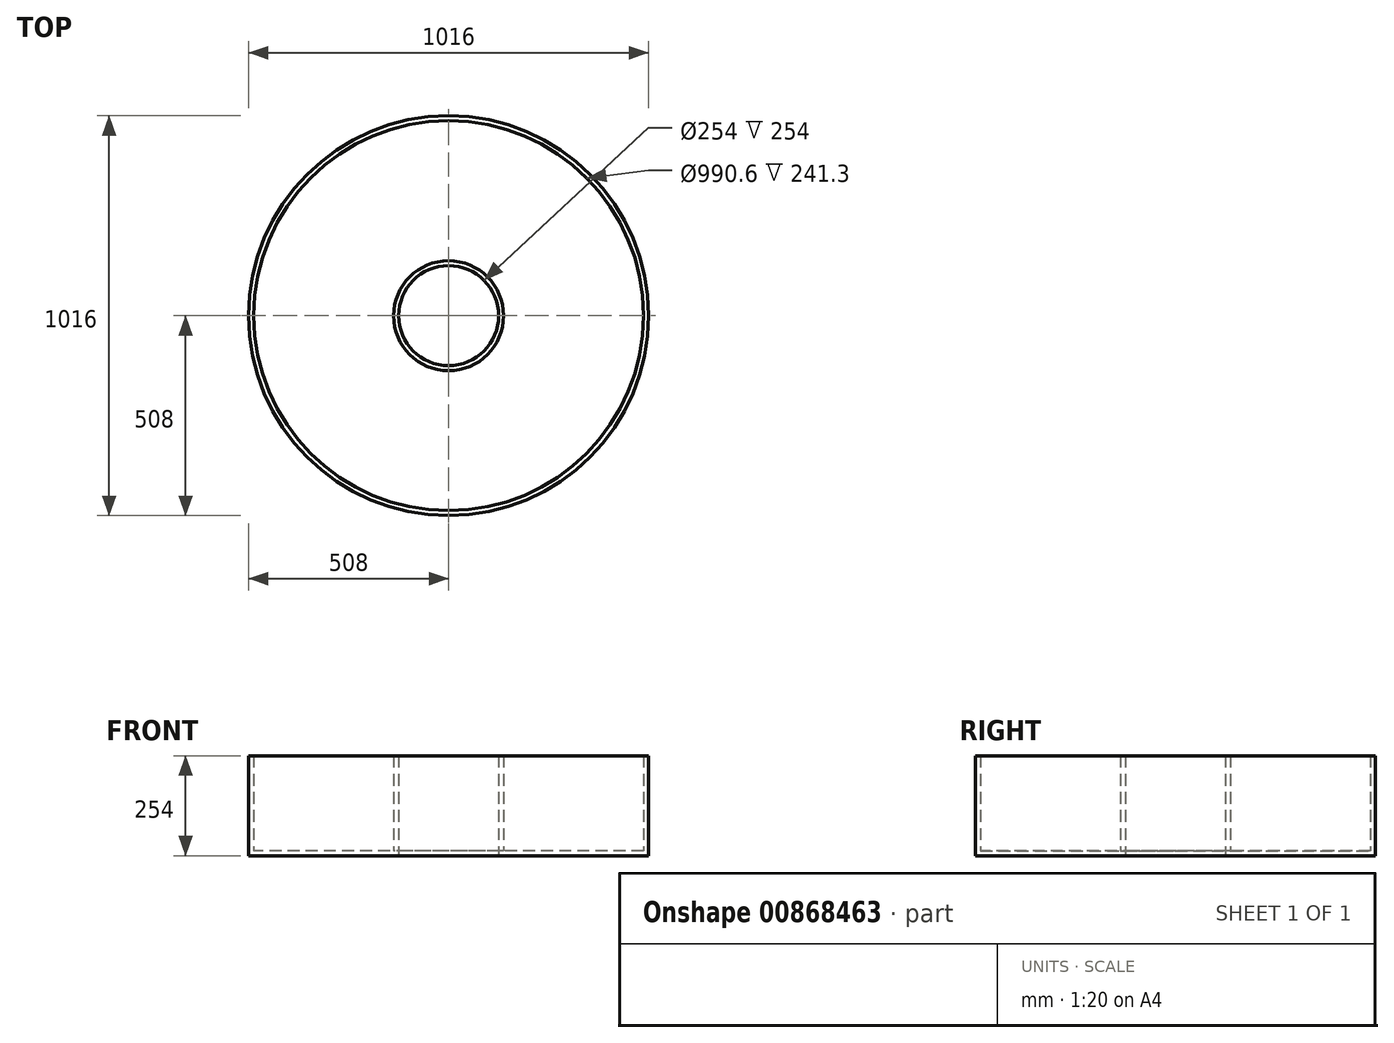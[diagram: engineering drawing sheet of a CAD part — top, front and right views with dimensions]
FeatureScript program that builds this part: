
annotation { "Feature Type Name" : "Feature", "Feature Type Description" : "" }
export const myFeature = defineFeature(function(context is Context, id is Id, definition is map)
    precondition{}
    {
        {
            var Q0;
            Q0=qCreatedBy(makeId("Top.planeOp"),FACE);
            var sketch = newSketch(context, id + "F0", { "sketchPlane" : qUnion([Q0])});
            skCircle(sketch, "E0", {"center": v(0, 0) * mm, "radius": 508 * mm});
            skCircle(sketch, "E1", {"center": v(0, 0) * mm, "radius": 127 * mm});
            skSolve(sketch);
        }
        {
            var Q0;
            Q0 = qSketchRegion(id + "F0", true);
            extrude(context, id + "F1", {"entities" : qUnion([Q0]), "depth" : 254 * mm, "offsetDistance" : 25.4 * mm});
        }
        {
            var Q0;
            Q0=makeQuery(id+"F1.opExtrude","CAP_FACE",FACE,{"disambiguationData":[OSD([sQuery(id+"F0.wireOp",EDGE,"E0"),sQuery(id+"F0.wireOp",EDGE,"E1")])],"isStart":false});
            shell(context, id + "F2", {"entities" : qUnion([Q0]), "thickness" : 12.7 * mm});
        }
    });
